# Revit family: Plumbing-Pipes-KOHLER-P_Trap-K-9000
name_source: partatom
category: Plumbing Fixtures
revit_build: Autodesk Revit 2015 (Build: 20140606_1530(x64)
units: mm (PartAtom-declared; Revit-internal decimal feet)

## types (1)
- CP-Polished Chrome
    ADA Compliant = No
    Assembly Code = C1030200
    CW Connection = No
    Cold Water Inlet = Cold Water Inlet
    Date Modified = 01/22/2019
    Default Elevation = 30"
    Description = Adjustable P-trap with tubing outlet, 1-1/2 inch x 1-1/2 inch
    Finish = Kohler-Metal-CP-Polished_Chrome
    Flow Rate = 0 GPM
    HW Connection = No
    Height = 4 7/8"
    Hot Water Inlet = Hot Water Inlet
    Length = 11 3/4"
    Manufacturer = KOHLER Co.
    MasterFormat 1995 = 154300
    MasterFormat 2004 = 22.11.00
    Material = Cast Brass Construction
    Model = K-9000-CP
    Pressure = 0.00 psi
    Product Documentation Link = https://www.us.kohler.com
    Product Name = P-Trap
    Product Page URL = http://www.us.kohler.com
    URL = https://www.us.kohler.com
    Vent Connection = No
    Waste Connection = Yes
    Waste Water Inlet = Waste Water Inlet
    Waste Water Outlet = Waste Water Outlet
    Width = 3"

## geometry (parser evidence)
native form markers: Sweep x5
no freeform markers — native parametric forms only
